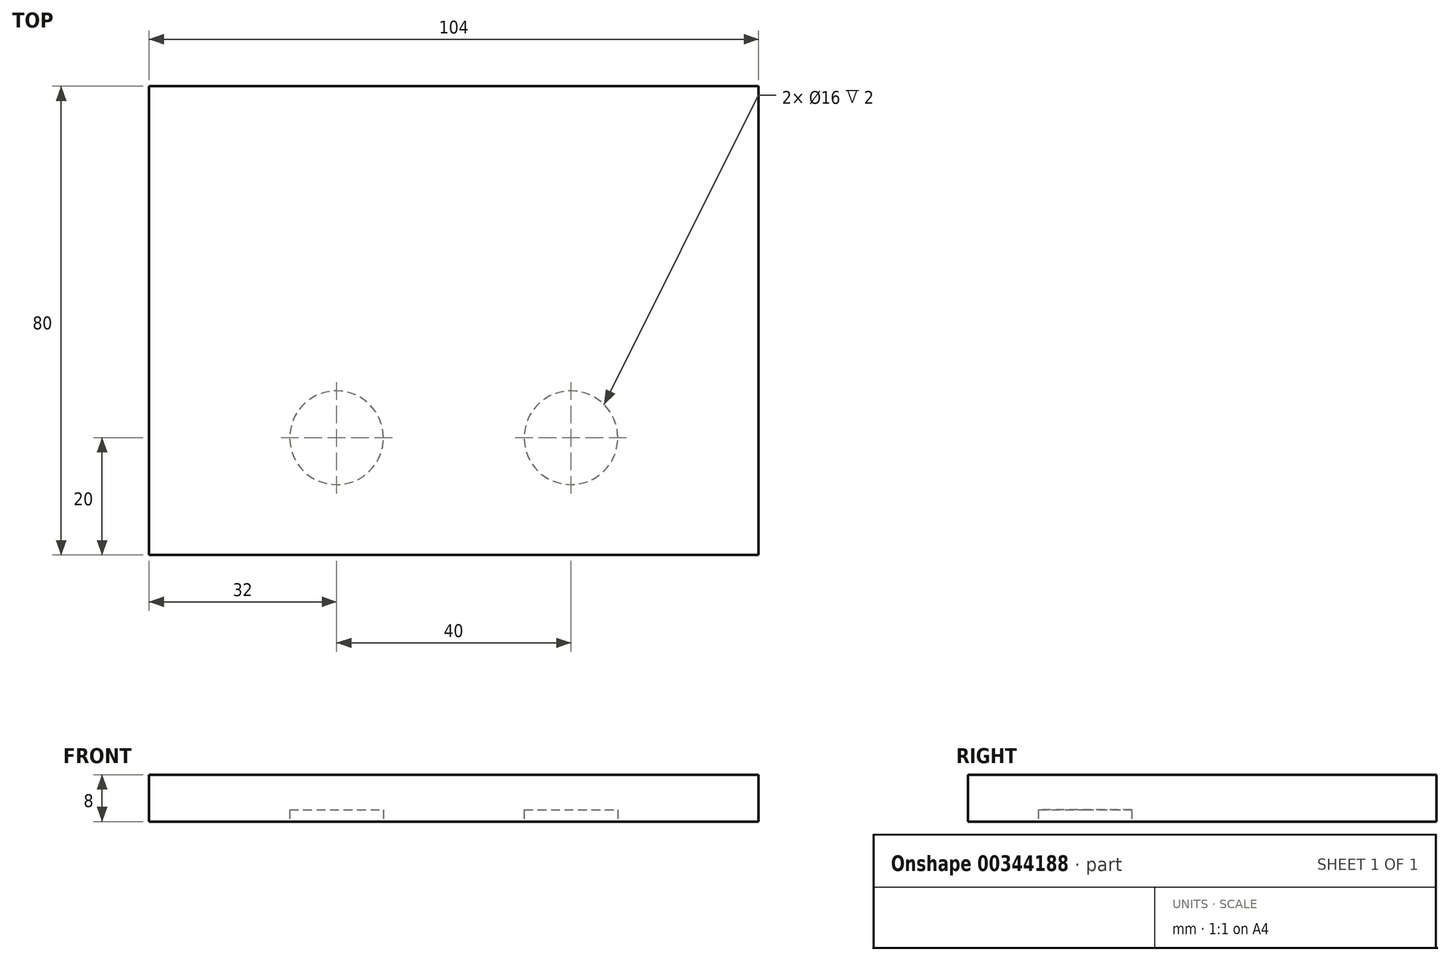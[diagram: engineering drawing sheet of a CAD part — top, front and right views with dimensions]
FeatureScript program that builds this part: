
annotation { "Feature Type Name" : "Feature", "Feature Type Description" : "" }
export const myFeature = defineFeature(function(context is Context, id is Id, definition is map)
    precondition{}
    {
        {
            var Q0;
            Q0=qCreatedBy(makeId("Top.planeOp"),FACE);
            var sketch = newSketch(context, id + "F0", { "sketchPlane" : qUnion([Q0])});
            skLineSegment(sketch, "E0.bottom", {"start": v(52, -40) * mm, "end": v(-52, -40) * mm});
            skLineSegment(sketch, "E0.top", {"start": v(52, 40) * mm, "end": v(-52, 40) * mm});
            skLineSegment(sketch, "E0.left", {"start": v(52, -40) * mm, "end": v(52, 40) * mm});
            skLineSegment(sketch, "E0.right", {"start": v(-52, -40) * mm, "end": v(-52, 40) * mm});
            skPoint(sketch, "E0.middle", {"position": v(0, 0) * mm});
            skSolve(sketch);
        }
        {
            var Q0;
            Q0 = qSketchRegion(id + "F0", true);
            extrude(context, id + "F1", {"entities" : qUnion([Q0]), "depth" : 8 * mm});
        }
        {
            var Q0;
            Q0=makeQuery(id+"F1.opExtrude","CAP_FACE",FACE,{"disambiguationData":[OSD([sQuery(id+"F0.wireOp",EDGE,"E0.bottom"),sQuery(id+"F0.wireOp",EDGE,"E0.top"),sQuery(id+"F0.wireOp",EDGE,"E0.left"),sQuery(id+"F0.wireOp",EDGE,"E0.right")])],"isStart":true});
            var sketch = newSketch(context, id + "F2", { "sketchPlane" : qUnion([Q0])});
            skLineSegment(sketch, "E1", {"start": v(-52.62, 20) * mm, "end": v(47.18, 20) * mm, "construction": true});
            skCircle(sketch, "E2", {"center": v(20, 20) * mm, "radius": 8 * mm});
            skCircle(sketch, "E3", {"center": v(-20, 20) * mm, "radius": 8 * mm});
            skSolve(sketch);
        }
        {
            var Q0;
            Q0 = qSketchRegion(id + "F2", true);
            extrude(context, id + "F3", {"entities" : qUnion([Q0]), "operationType" : NewBodyOperationType.REMOVE, "oppositeDirection" : true, "depth" : 2 * mm});
        }
    });
